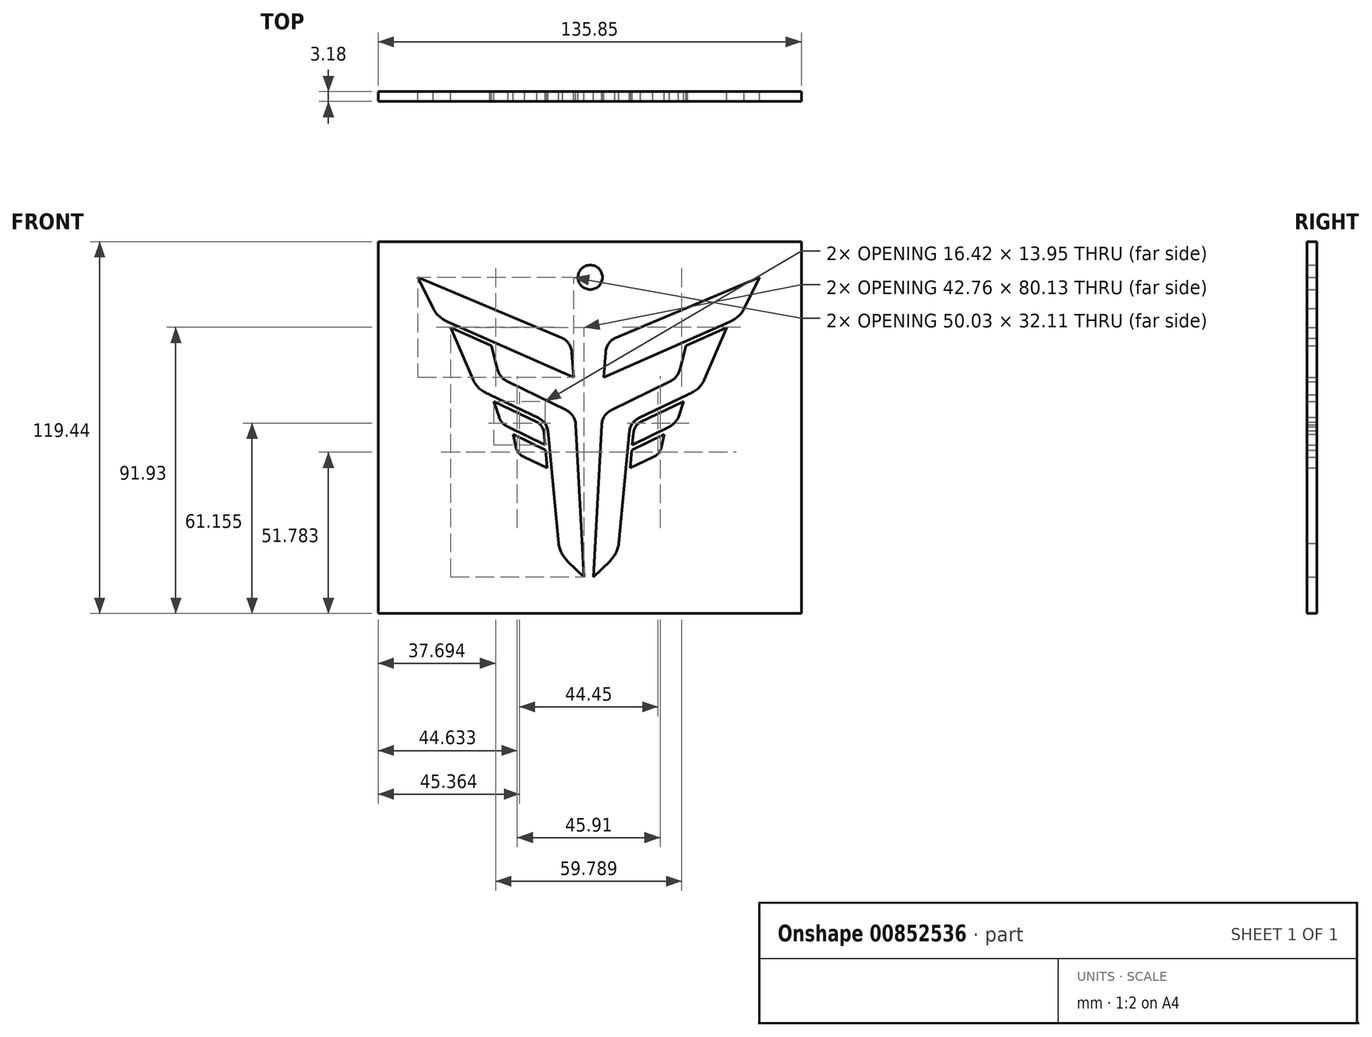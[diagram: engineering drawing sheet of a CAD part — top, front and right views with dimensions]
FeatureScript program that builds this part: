
annotation { "Feature Type Name" : "Feature", "Feature Type Description" : "" }
export const myFeature = defineFeature(function(context is Context, id is Id, definition is map)
    precondition{}
    {
        {
            var Q0;
            Q0=qCreatedBy(makeId("Front.planeOp"),FACE);
            var sketch = newSketch(context, id + "F0", { "sketchPlane" : qUnion([Q0])});
            skLineSegment(sketch, "E0", {"start": v(4.4, 15.87) * mm, "end": v(45, 33.78) * mm, "construction": true});
            skArc(sketch, "E1", {"start": v(45, 33.78) * mm, "mid": v(47.59, 35.5) * mm, "end": v(49.46, 37.97) * mm});
            skLineSegment(sketch, "E2", {"start": v(54.43, 47.97) * mm, "end": v(49.46, 37.97) * mm});
            skLineSegment(sketch, "E3", {"start": v(54.43, 47.97) * mm, "end": v(7.95, 28.45) * mm});
            skLineSegment(sketch, "E4", {"start": v(4.4, 15.87) * mm, "end": v(4.94, 23.8) * mm});
            skArc(sketch, "E5", {"start": v(7.95, 28.45) * mm, "mid": v(5.85, 26.52) * mm, "end": v(4.94, 23.8) * mm});
            skLineSegment(sketch, "E6", {"start": v(30.74, 26.03) * mm, "end": v(43.85, 31.84) * mm});
            skLineSegment(sketch, "E7", {"start": v(43.85, 31.84) * mm, "end": v(36.77, 15.32) * mm});
            skLineSegment(sketch, "E8", {"start": v(30.74, 26.03) * mm, "end": v(28.84, 18.47) * mm});
            skArc(sketch, "E9", {"start": v(25.47, 14.48) * mm, "mid": v(27.62, 16.08) * mm, "end": v(28.84, 18.47) * mm});
            skArc(sketch, "E10", {"start": v(31.24, 10.3) * mm, "mid": v(34.55, 12.21) * mm, "end": v(36.77, 15.32) * mm});
            skLineSegment(sketch, "E11", {"start": v(31.24, 10.3) * mm, "end": v(15.54, 2.7) * mm});
            skLineSegment(sketch, "E12", {"start": v(25.47, 14.48) * mm, "end": v(6.7, 5.26) * mm});
            skArc(sketch, "E13", {"start": v(6.7, 5.26) * mm, "mid": v(4.56, 3.36) * mm, "end": v(3.69, 0.63) * mm});
            skArc(sketch, "E14", {"start": v(15.54, 2.7) * mm, "mid": v(13.6, 1.07) * mm, "end": v(12.61, -1.27) * mm});
            skLineSegment(sketch, "E15", {"start": v(3.69, 0.63) * mm, "end": v(1.1, -48.3) * mm});
            skLineSegment(sketch, "E16", {"start": v(1.1, -48.3) * mm, "end": v(6.21, -43.31) * mm});
            skArc(sketch, "E17", {"start": v(6.21, -43.31) * mm, "mid": v(8.18, -40.66) * mm, "end": v(9.2, -37.5) * mm});
            skLineSegment(sketch, "E18", {"start": v(12.61, -1.27) * mm, "end": v(9.2, -37.5) * mm});
            skLineSegment(sketch, "E19", {"start": v(13.38, -7.54) * mm, "end": v(23.73, -2.43) * mm});
            skLineSegment(sketch, "E20", {"start": v(13.38, -7.54) * mm, "end": v(12.84, -13.23) * mm});
            skLineSegment(sketch, "E21", {"start": v(12.84, -13.23) * mm, "end": v(20.08, -9.8) * mm});
            skLineSegment(sketch, "E22", {"start": v(23.73, -2.43) * mm, "end": v(22.93, -6.48) * mm});
            skArc(sketch, "E23", {"start": v(20.08, -9.8) * mm, "mid": v(21.94, -8.51) * mm, "end": v(22.93, -6.48) * mm});
            skLineSegment(sketch, "E24", {"start": v(13.53, -5.83) * mm, "end": v(25.38, 0) * mm});
            skLineSegment(sketch, "E25", {"start": v(13.53, -5.83) * mm, "end": v(13.9, -1.94) * mm});
            skArc(sketch, "E26", {"start": v(16.2, 1.5) * mm, "mid": v(14.62, 0.08) * mm, "end": v(13.9, -1.94) * mm});
            skLineSegment(sketch, "E27", {"start": v(16.2, 1.5) * mm, "end": v(29.95, 8.12) * mm});
            skLineSegment(sketch, "E28", {"start": v(29.95, 8.12) * mm, "end": v(28.28, 2.99) * mm});
            skLineSegment(sketch, "E29.MirrorCS", {"start": v(-14.5, -5.83) * mm, "end": v(-26.34, 0) * mm});
            skArc(sketch, "E30.MirrorCS", {"start": v(-21.04, -9.8) * mm, "mid": v(-22.9, -8.51) * mm, "end": v(-23.9, -6.48) * mm});
            skLineSegment(sketch, "E31.MirrorCS", {"start": v(-24.69, -2.43) * mm, "end": v(-23.9, -6.48) * mm});
            skLineSegment(sketch, "E32.MirrorCS", {"start": v(-14.34, -7.54) * mm, "end": v(-13.8, -13.23) * mm});
            skArc(sketch, "E33.MirrorCS", {"start": v(-26.43, 14.48) * mm, "mid": v(-28.58, 16.08) * mm, "end": v(-29.8, 18.47) * mm});
            skArc(sketch, "E34.MirrorCS", {"start": v(-8.92, 28.45) * mm, "mid": v(-6.8, 26.52) * mm, "end": v(-5.9, 23.8) * mm});
            skArc(sketch, "E35.MirrorCS", {"start": v(-17.17, 1.5) * mm, "mid": v(-15.58, 0.08) * mm, "end": v(-14.86, -1.94) * mm});
            skArc(sketch, "E36.MirrorCS", {"start": v(-45.97, 33.78) * mm, "mid": v(-48.55, 35.5) * mm, "end": v(-50.42, 37.97) * mm});
            skArc(sketch, "E37.MirrorCS", {"start": v(-7.18, -43.31) * mm, "mid": v(-9.14, -40.66) * mm, "end": v(-10.16, -37.5) * mm});
            skArc(sketch, "E38.MirrorCS", {"start": v(-16.5, 2.7) * mm, "mid": v(-14.55, 1.07) * mm, "end": v(-13.58, -1.27) * mm});
            skLineSegment(sketch, "E39.MirrorCS", {"start": v(-14.5, -5.83) * mm, "end": v(-14.86, -1.94) * mm});
            skLineSegment(sketch, "E40.MirrorCS", {"start": v(-14.34, -7.54) * mm, "end": v(-24.69, -2.43) * mm});
            skLineSegment(sketch, "E41.MirrorCS", {"start": v(-30.92, 8.12) * mm, "end": v(-29.24, 2.99) * mm});
            skLineSegment(sketch, "E42.MirrorCS", {"start": v(-31.7, 26.03) * mm, "end": v(-29.8, 18.47) * mm});
            skLineSegment(sketch, "E43.MirrorCS", {"start": v(-32.2, 10.3) * mm, "end": v(-16.5, 2.7) * mm});
            skLineSegment(sketch, "E44.MirrorCS", {"start": v(-13.8, -13.23) * mm, "end": v(-21.04, -9.8) * mm});
            skLineSegment(sketch, "E45.MirrorCS", {"start": v(-13.58, -1.27) * mm, "end": v(-10.16, -37.5) * mm});
            skLineSegment(sketch, "E46.MirrorCS", {"start": v(-5.36, 15.87) * mm, "end": v(-45.97, 33.78) * mm, "construction": true});
            skArc(sketch, "E47.MirrorCS", {"start": v(-32.2, 10.3) * mm, "mid": v(-35.52, 12.21) * mm, "end": v(-37.74, 15.32) * mm});
            skArc(sketch, "E48.MirrorCS", {"start": v(-7.66, 5.26) * mm, "mid": v(-5.52, 3.36) * mm, "end": v(-4.65, 0.63) * mm});
            skLineSegment(sketch, "E49.MirrorCS", {"start": v(-17.17, 1.5) * mm, "end": v(-30.92, 8.12) * mm});
            skLineSegment(sketch, "E50.MirrorCS", {"start": v(-5.36, 15.87) * mm, "end": v(-5.9, 23.8) * mm});
            skLineSegment(sketch, "E51.MirrorCS", {"start": v(-44.82, 31.84) * mm, "end": v(-37.74, 15.32) * mm});
            skLineSegment(sketch, "E52.MirrorCS", {"start": v(-26.43, 14.48) * mm, "end": v(-7.66, 5.26) * mm});
            skLineSegment(sketch, "E53.MirrorCS", {"start": v(-31.7, 26.03) * mm, "end": v(-44.82, 31.84) * mm});
            skLineSegment(sketch, "E54.MirrorCS", {"start": v(-4.65, 0.63) * mm, "end": v(-2.06, -48.3) * mm});
            skLineSegment(sketch, "E55", {"start": v(-50.42, 37.97) * mm, "end": v(-55.4, 47.97) * mm});
            skLineSegment(sketch, "E56", {"start": v(-55.4, 47.97) * mm, "end": v(-8.92, 28.45) * mm});
            skArc(sketch, "E57", {"start": v(25.38, 0) * mm, "mid": v(27.09, 1.24) * mm, "end": v(28.28, 2.99) * mm});
            skArc(sketch, "E58", {"start": v(-29.24, 2.99) * mm, "mid": v(-28.14, 1.16) * mm, "end": v(-26.34, 0) * mm});
            skLineSegment(sketch, "E59", {"start": v(-5.36, 15.87) * mm, "end": v(-45.97, 33.78) * mm});
            skLineSegment(sketch, "E60", {"start": v(4.4, 15.87) * mm, "end": v(45, 33.78) * mm});
            skLineSegment(sketch, "E61", {"start": v(-7.18, -43.31) * mm, "end": v(-2.06, -48.3) * mm});
            skLineSegment(sketch, "E62.bottom", {"start": v(-68.07, 59.43) * mm, "end": v(67.78, 59.43) * mm});
            skLineSegment(sketch, "E62.top", {"start": v(-68.07, -60) * mm, "end": v(67.78, -60) * mm});
            skLineSegment(sketch, "E62.left", {"start": v(-68.07, 59.43) * mm, "end": v(-68.07, -60) * mm});
            skLineSegment(sketch, "E62.right", {"start": v(67.78, 59.43) * mm, "end": v(67.78, -60) * mm});
            skCircle(sketch, "E63", {"center": v(0, 47.97) * mm, "radius": 3.93 * mm});
            skPoint(sketch, "E63.centerSnap0", {"position": v(-0.48, 47.97) * mm});
            skSolve(sketch);
        }
        {
            var Q0;
            Q0 = qSketchRegion(id + "F0", true);
            extrude(context, id + "F1", {"entities" : qUnion([Q0]), "depth" : 3.17 * mm, "offsetDistance" : 25.4 * mm});
        }
    });
